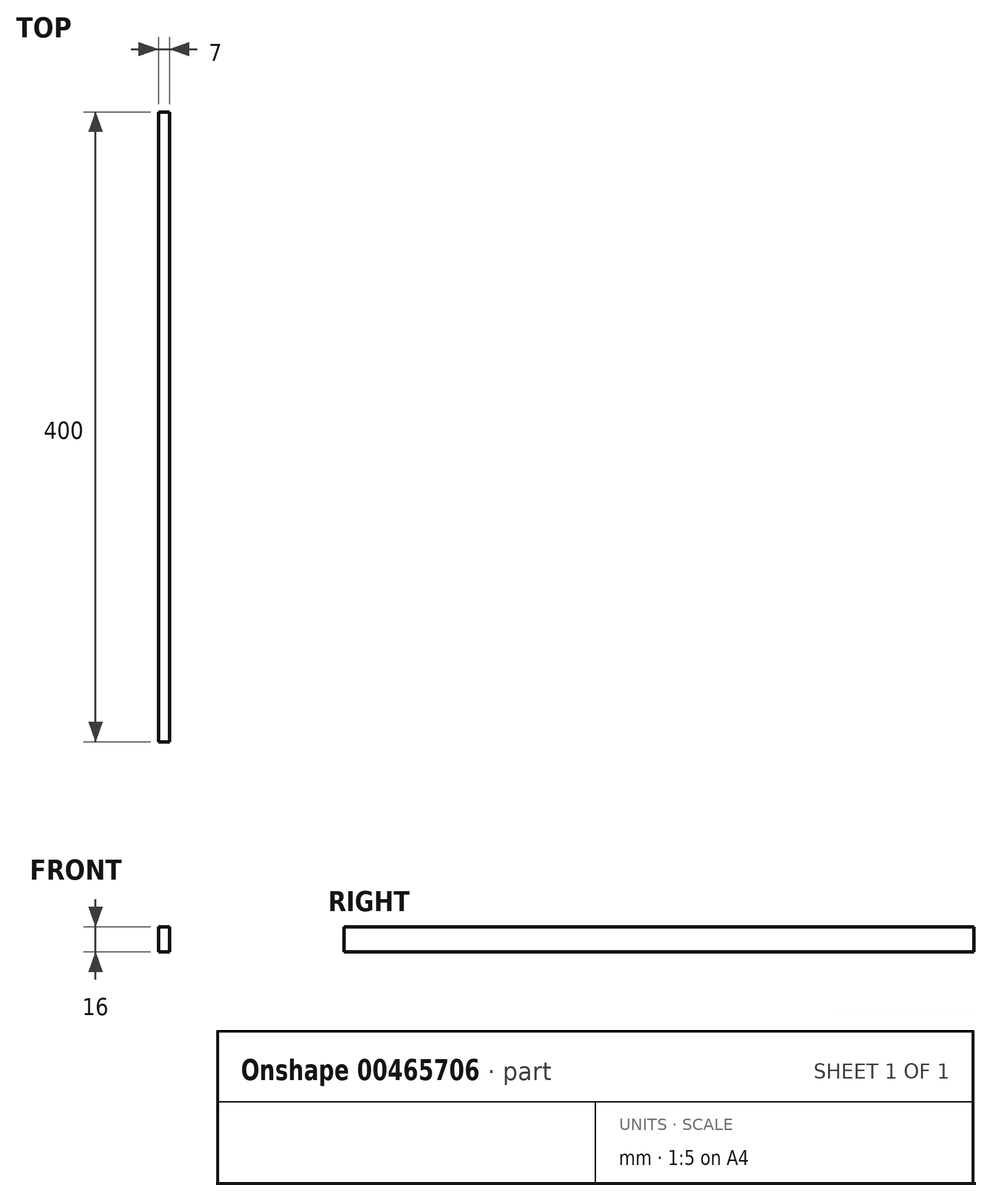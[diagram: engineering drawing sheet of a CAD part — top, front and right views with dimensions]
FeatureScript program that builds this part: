
annotation { "Feature Type Name" : "Feature", "Feature Type Description" : "" }
export const myFeature = defineFeature(function(context is Context, id is Id, definition is map)
    precondition{}
    {
        {
            var Q0;
            Q0=qCreatedBy(makeId("Front.planeOp"),FACE);
            var sketch = newSketch(context, id + "F0", { "sketchPlane" : qUnion([Q0])});
            skLineSegment(sketch, "E0", {"start": v(0, 0) * mm, "end": v(18, 0) * mm});
            skLineSegment(sketch, "E1", {"start": v(18, -106) * mm, "end": v(18, 0) * mm});
            skLineSegment(sketch, "E2", {"start": v(18, -106) * mm, "end": v(11, -106) * mm});
            skLineSegment(sketch, "E3", {"start": v(11, -106) * mm, "end": v(11, -90) * mm});
            skLineSegment(sketch, "E4", {"start": v(11, -90) * mm, "end": v(18, -90) * mm});
            skLineSegment(sketch, "E5", {"start": v(18, 30) * mm, "end": v(21, 30) * mm});
            skLineSegment(sketch, "E6", {"start": v(18, 30) * mm, "end": v(18, 134) * mm});
            skLineSegment(sketch, "E7", {"start": v(18, 134) * mm, "end": v(11, 134) * mm});
            skLineSegment(sketch, "E8", {"start": v(11, 134) * mm, "end": v(11, 150) * mm});
            skLineSegment(sketch, "E9", {"start": v(11, 150) * mm, "end": v(18, 150) * mm});
            skLineSegment(sketch, "E10", {"start": v(18, 150) * mm, "end": v(18, 254) * mm});
            skLineSegment(sketch, "E11", {"start": v(18, 254) * mm, "end": v(11, 254) * mm});
            skLineSegment(sketch, "E12", {"start": v(11, 254) * mm, "end": v(11, 270) * mm});
            skLineSegment(sketch, "E13", {"start": v(11, 270) * mm, "end": v(18, 270) * mm});
            skLineSegment(sketch, "E14", {"start": v(18, 270) * mm, "end": v(18, 374) * mm});
            skLineSegment(sketch, "E15", {"start": v(18, 374) * mm, "end": v(11, 374) * mm});
            skLineSegment(sketch, "E16", {"start": v(11, 374) * mm, "end": v(11, 390) * mm});
            skLineSegment(sketch, "E17", {"start": v(11, 390) * mm, "end": v(18, 390) * mm});
            skLineSegment(sketch, "E18", {"start": v(18, 390) * mm, "end": v(18, 494) * mm});
            skLineSegment(sketch, "E19", {"start": v(18, 494) * mm, "end": v(11, 494) * mm});
            skLineSegment(sketch, "E20", {"start": v(11, 494) * mm, "end": v(11, 510) * mm});
            skLineSegment(sketch, "E21", {"start": v(11, 510) * mm, "end": v(18, 510) * mm});
            skLineSegment(sketch, "E22", {"start": v(18, 510) * mm, "end": v(18, 614) * mm});
            skLineSegment(sketch, "E23", {"start": v(18, 614) * mm, "end": v(11, 614) * mm});
            skLineSegment(sketch, "E24", {"start": v(11, 614) * mm, "end": v(11, 630) * mm});
            skLineSegment(sketch, "E25", {"start": v(11, 630) * mm, "end": v(18, 630) * mm});
            skLineSegment(sketch, "E26", {"start": v(18, 630) * mm, "end": v(18, 734) * mm});
            skLineSegment(sketch, "E27", {"start": v(18, 734) * mm, "end": v(11, 734) * mm});
            skLineSegment(sketch, "E28", {"start": v(11, 734) * mm, "end": v(11, 750) * mm});
            skLineSegment(sketch, "E29", {"start": v(11, 750) * mm, "end": v(18, 750) * mm});
            skLineSegment(sketch, "E30", {"start": v(18, 750) * mm, "end": v(18, 854) * mm});
            skLineSegment(sketch, "E31", {"start": v(18, 854) * mm, "end": v(11, 854) * mm});
            skLineSegment(sketch, "E32", {"start": v(11, 854) * mm, "end": v(11, 870) * mm});
            skLineSegment(sketch, "E33", {"start": v(11, 870) * mm, "end": v(18, 870) * mm});
            skLineSegment(sketch, "E34", {"start": v(18, 870) * mm, "end": v(18, 974) * mm});
            skLineSegment(sketch, "E35", {"start": v(18, 974) * mm, "end": v(11, 974) * mm});
            skLineSegment(sketch, "E36", {"start": v(11, 974) * mm, "end": v(11, 990) * mm});
            skLineSegment(sketch, "E37", {"start": v(11, 990) * mm, "end": v(18, 990) * mm});
            skLineSegment(sketch, "E38", {"start": v(18, 990) * mm, "end": v(18, 1000) * mm});
            skLineSegment(sketch, "E39", {"start": v(0, 0) * mm, "end": v(0, 1000) * mm});
            skLineSegment(sketch, "E40", {"start": v(18, 1000) * mm, "end": v(0, 1000) * mm});
            skSolve(sketch);
        }
        {
            var Q0;
            Q0 = qSketchRegion(id + "F0", true);
            extrude(context, id + "F1", {"entities" : qUnion([Q0]), "depth" : 400 * mm});
        }
    });
